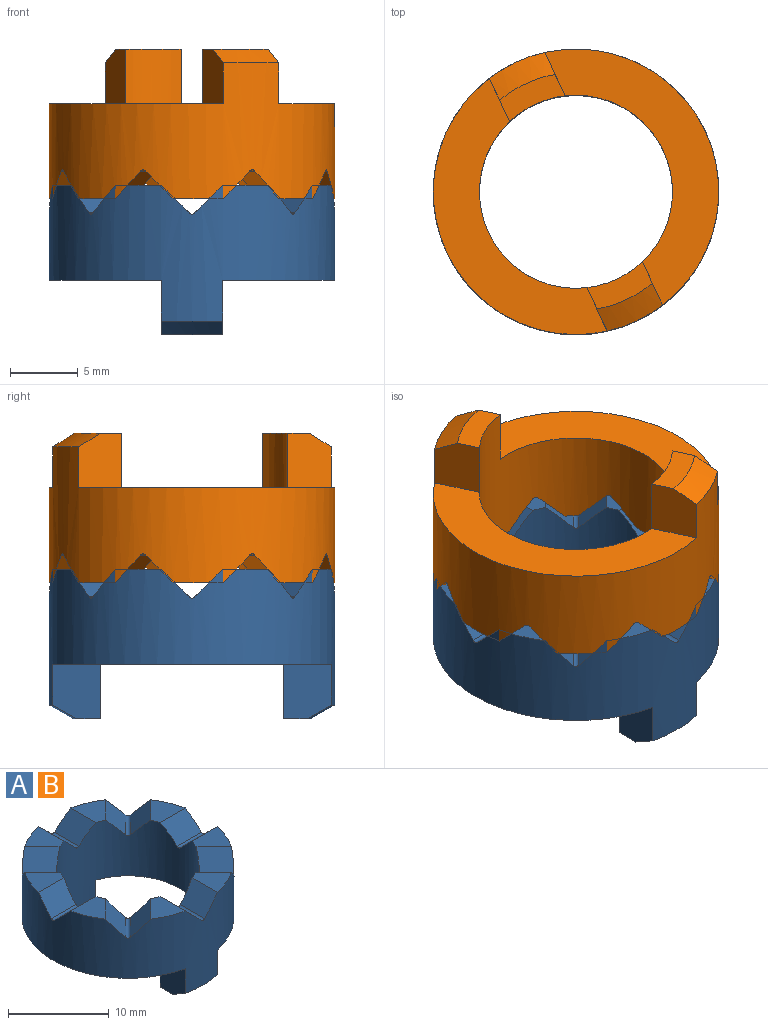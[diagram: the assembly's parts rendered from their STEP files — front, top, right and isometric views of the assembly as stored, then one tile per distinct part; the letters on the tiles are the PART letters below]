
ASSEMBLY  parts=2 mates=1
PART A: 44 faces, bbox 21x21x11 mm
  f0: cylinder r=10.5mm len=21mm, axis (0,0,1), area 448.4mm2, adj f1,f2,f3,f4,f5,f6,f7,f11
  f1: plane 3.9x3.41mm, normal (0,0,1), area 8mm2, adj f0,f8,f40,f42
  f2: plane 3.9x3.41mm, normal (0,0,1), area 8mm2, adj f0,f8,f37,f39
  f3: plane 3.9x3.41mm, normal (0,0,1), area 8mm2, adj f0,f8,f34,f36
  f4: plane 3.9x3.41mm, normal (0,0,1), area 8mm2, adj f0,f8,f31,f33
  f5: plane 3.9x3.41mm, normal (0,0,1), area 8mm2, adj f0,f8,f28,f30
  f6: plane 3.9x3.41mm, normal (0,0,1), area 8mm2, adj f0,f8,f25,f27
  f7: plane 3.9x3.41mm, normal (0,0,1), area 8mm2, adj f0,f8,f22,f24
  f8: cylinder r=7.1mm len=14.2mm, axis (0,0,1), area 308.2mm2, adj f1,f2,f3,f4,f5,f6,f7,f9
  f9: plane 4.5x2.03mm, normal (0,0,-1), area 7.6mm2, adj f8,f12,f15,f19
  f10: plane 4.5x2.03mm, normal (0,0,-1), area 7.6mm2, adj f8,f13,f16,f18
  f11: plane 3.9x3.41mm, normal (0,0,1), area 8mm2, adj f0,f8,f21,f43
  f12: plane 4x3.52mm, normal (1,0,0), area 13.2mm2, adj f0,f8,f9,f14,f19
  f13: plane 4x3.52mm, normal (1,0,0), area 13.2mm2, adj f0,f8,f10,f14,f18
  f14: plane 20.51x8.25mm, normal (0,0,-1), area 78.5mm2, adj f0,f8,f12,f13
  f15: plane 4x3.52mm, normal (-1,0,0), area 13.2mm2, adj f0,f8,f9,f17,f19
  f16: plane 4x3.52mm, normal (-1,0,0), area 13.2mm2, adj f0,f8,f10,f17,f18
  f17: plane 20.51x8.25mm, normal (0,0,-1), area 78.5mm2, adj f0,f8,f15,f16
  f18: cone r=10.5mm half-angle=60deg, axis (0,0,1), area 9.1mm2, adj f0,f10,f13,f16
  f19: cone r=10.5mm half-angle=60deg, axis (0,0,1), area 9.1mm2, adj f0,f9,f12,f15
  f20: cylinder r=0.3mm len=3.4mm, axis (1,0,0), area 1.6mm2, adj f0,f8,f21,f22
  f21: plane 3.78x2.05mm, normal (0,0.71,0.71), area 9.9mm2, adj f0,f8,f11,f20
  f22: plane 3.78x2.05mm, normal (0,-0.71,0.71), area 9.9mm2, adj f0,f7,f8,f20
  f23: cylinder r=0.3mm len=2.71mm, axis (0.71,-0.71,0), area 1.6mm2, adj f0,f8,f24,f25
  f24: plane 4.11x3.69mm, normal (0.5,0.5,0.71), area 9.9mm2, adj f0,f7,f8,f23
  f25: plane 4.11x3.69mm, normal (-0.5,-0.5,0.71), area 9.9mm2, adj f0,f6,f8,f23
  f26: cylinder r=0.3mm len=3.4mm, axis (0,-1,0), area 1.6mm2, adj f0,f8,f27,f28
  f27: plane 3.78x2.05mm, normal (0.71,0,0.71), area 9.9mm2, adj f0,f6,f8,f26
  f28: plane 3.78x2.05mm, normal (-0.71,0,0.71), area 9.9mm2, adj f0,f5,f8,f26
  f29: cylinder r=0.3mm len=2.71mm, axis (-0.71,-0.71,0), area 1.6mm2, adj f0,f8,f30,f31
  f30: plane 4.11x3.69mm, normal (0.5,-0.5,0.71), area 9.9mm2, adj f0,f5,f8,f29
  f31: plane 4.11x3.69mm, normal (-0.5,0.5,0.71), area 9.9mm2, adj f0,f4,f8,f29
  f32: cylinder r=0.3mm len=3.4mm, axis (-1,0,0), area 1.6mm2, adj f0,f8,f33,f34
  f33: plane 3.78x2.05mm, normal (0,-0.71,0.71), area 9.9mm2, adj f0,f4,f8,f32
  f34: plane 3.78x2.05mm, normal (0,0.71,0.71), area 9.9mm2, adj f0,f3,f8,f32
  f35: cylinder r=0.3mm len=2.71mm, axis (-0.71,0.71,0), area 1.6mm2, adj f0,f8,f36,f37
  f36: plane 4.11x3.69mm, normal (-0.5,-0.5,0.71), area 9.9mm2, adj f0,f3,f8,f35
  f37: plane 4.11x3.69mm, normal (0.5,0.5,0.71), area 9.9mm2, adj f0,f2,f8,f35
  f38: cylinder r=0.3mm len=3.4mm, axis (0,1,0), area 1.6mm2, adj f0,f8,f39,f40
  f39: plane 3.78x2.05mm, normal (-0.71,0,0.71), area 9.9mm2, adj f0,f2,f8,f38
  f40: plane 3.78x2.05mm, normal (0.71,0,0.71), area 9.9mm2, adj f0,f1,f8,f38
  f41: cylinder r=0.3mm len=2.71mm, axis (0.71,0.71,0), area 1.6mm2, adj f0,f8,f42,f43
  f42: plane 4.11x3.69mm, normal (-0.5,0.5,0.71), area 9.9mm2, adj f0,f1,f8,f41
  f43: plane 4.11x3.69mm, normal (0.5,-0.5,0.71), area 9.9mm2, adj f0,f8,f11,f41
PART B: same geometry as A
PLACE A t=(-0.06,4.63,5.49)mm
PLACE B rot(axis=(0.98,0.22,0),180deg) t=(-0.06,4.63,4.49)mm
MATE revolute B.f0 <-> A.f0  axis (0,0,-1) through (-0.06,4.63,9.99)mm
